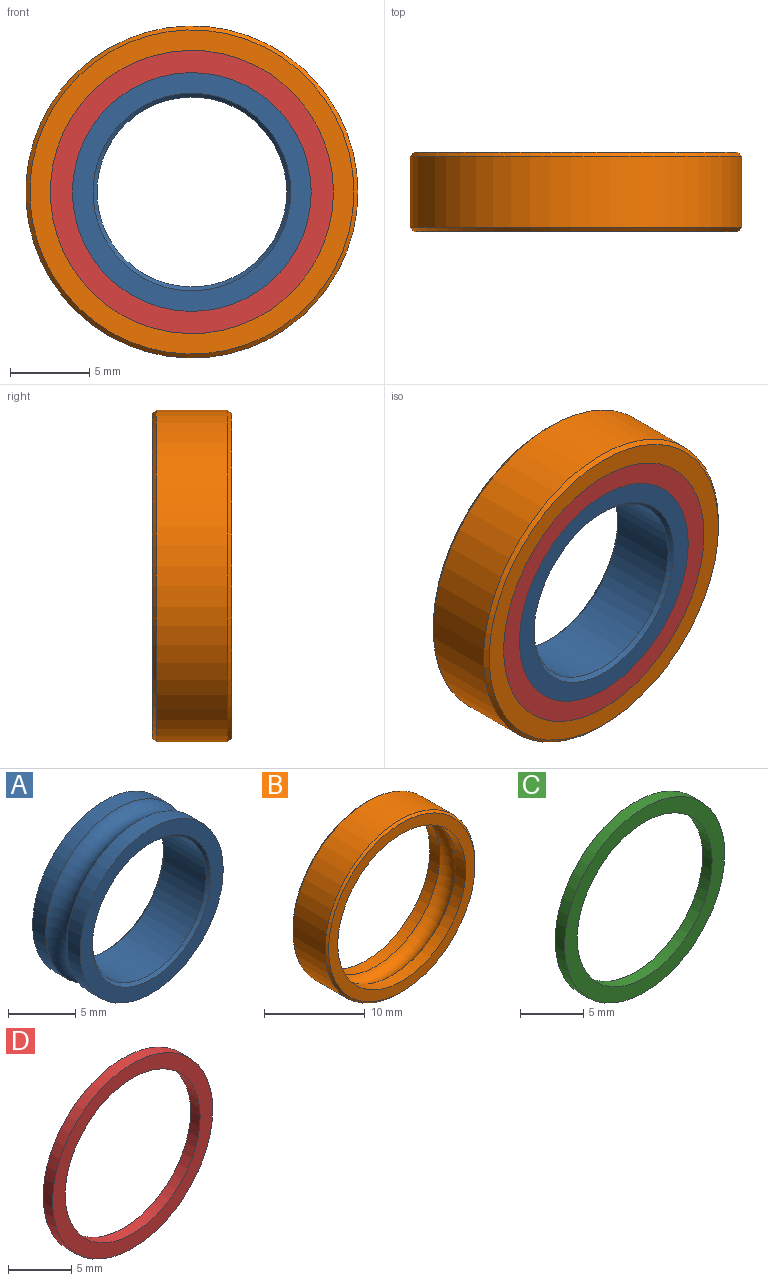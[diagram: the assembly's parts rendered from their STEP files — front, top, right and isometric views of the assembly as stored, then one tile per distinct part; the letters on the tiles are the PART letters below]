
ASSEMBLY  parts=4 mates=3
PART A: 8 faces, bbox 17.9x5x17.9 mm
  f0: torus R=8.25mm, axis (0,-1,0), area 118.9mm2, adj f4,f5
  f1: cone r=6.25mm half-angle=45deg, axis (0,-1,0), area 13.6mm2, adj f2,f6
  f2: cylinder r=6mm len=12mm, axis (0,-1,0), area 169.6mm2, adj f1,f3
  f3: cone r=6mm half-angle=45deg, axis (0,1,0), area 13.6mm2, adj f2,f7
  f4: cylinder r=7.55mm len=15.09mm, axis (0,-1,0), area 65.9mm2, adj f0,f7
  f5: cylinder r=7.55mm len=15.09mm, axis (0,-1,0), area 65.9mm2, adj f0,f6
  f6: plane 15.09x15.09mm, normal (0,-1,0), area 56.2mm2, adj f1,f5
  f7: plane 15.09x15.09mm, normal (0,1,0), area 56.2mm2, adj f3,f4
PART B: 8 faces, bbox 21x5x21 mm
  f0: cylinder r=8.95mm len=17.91mm, axis (0,-1,0), area 78.1mm2, adj f1,f7
  f1: torus R=8.25mm, axis (0,-1,0), area 155.6mm2, adj f0,f2
  f2: cylinder r=8.95mm len=17.91mm, axis (0,-1,0), area 78.1mm2, adj f1,f6
  f3: cone r=10.25mm half-angle=45deg, axis (0,-1,0), area 23mm2, adj f4,f6
  f4: cylinder r=10.5mm len=21mm, axis (0,-1,0), area 296.9mm2, adj f3,f5
  f5: cone r=10.5mm half-angle=45deg, axis (0,1,0), area 23mm2, adj f4,f7
  f6: plane 20.5x20.5mm, normal (0,1,0), area 78.2mm2, adj f2,f3
  f7: plane 20.5x20.5mm, normal (0,-1,0), area 78.2mm2, adj f0,f5
PART C: 4 faces, bbox 17.9x1.1x17.9 mm
  f0: cylinder r=8.95mm len=17.91mm, axis (0,-1,0), area 59.6mm2, adj f2,f3
  f1: cylinder r=7.55mm len=15.09mm, axis (0,-1,0), area 50.3mm2, adj f2,f3
  f2: plane 17.91x17.91mm, normal (0,1,0), area 72.9mm2, adj f0,f1
  f3: plane 17.91x17.91mm, normal (0,-1,0), area 72.9mm2, adj f0,f1
PART D: 4 faces, bbox 17.9x1.1x17.9 mm
  f0: cylinder r=8.95mm len=17.91mm, axis (0,-1,0), area 59.6mm2, adj f2,f3
  f1: cylinder r=7.55mm len=15.09mm, axis (0,-1,0), area 50.3mm2, adj f2,f3
  f2: plane 17.91x17.91mm, normal (0,-1,0), area 72.9mm2, adj f0,f1
  f3: plane 17.91x17.91mm, normal (0,1,0), area 72.9mm2, adj f0,f1
PLACE A t=(-8.98,-7.04,-2.79)mm fixed
PLACE B t=(-8.98,-7.04,-2.79)mm
PLACE C t=(-8.98,-6.92,-2.79)mm
PLACE D t=(-8.98,-7.17,-2.79)mm
MATE fastened B.f0 <-> A.f0  axis (0,-1,0) through (-8.98,-9.54,-2.79)mm
MATE fastened D.f0 <-> B.f0  axis (0,-1,0) through (-8.98,-9.54,-2.79)mm
MATE fastened C.f0 <-> B.f0  axis (0,1,0) through (-8.98,-4.54,-2.79)mm
